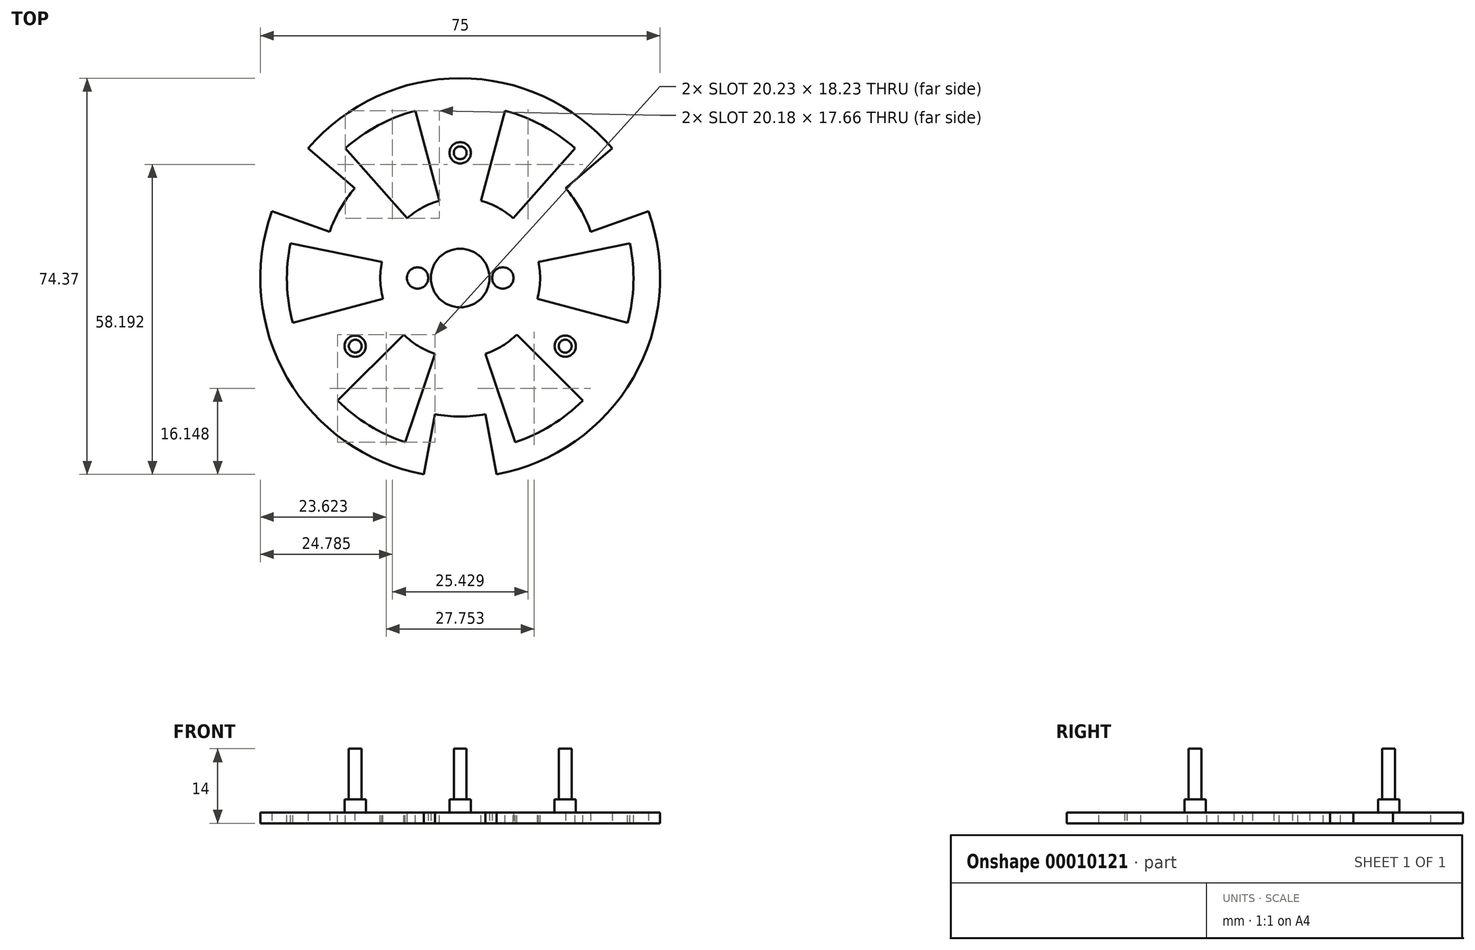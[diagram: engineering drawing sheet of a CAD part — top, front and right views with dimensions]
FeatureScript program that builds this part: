
annotation { "Feature Type Name" : "Feature", "Feature Type Description" : "" }
export const myFeature = defineFeature(function(context is Context, id is Id, definition is map)
    precondition{}
    {
        {
            var Q0;
            Q0=qCreatedBy(makeId("Top.planeOp"),FACE);
            var sketch = newSketch(context, id + "F0", { "sketchPlane" : qUnion([Q0])});
            skArc(sketch, "E0", {"start": v(6.83, -36.87) * mm, "mid": v(32.48, -18.75) * mm, "end": v(35.35, 12.52) * mm});
            skCircle(sketch, "E1", {"center": v(0, 0) * mm, "radius": 5.5 * mm});
            skLineSegment(sketch, "E2", {"start": v(0, 0) * mm, "end": v(-4.74, -25.56) * mm, "construction": true});
            skLineSegment(sketch, "E3", {"start": v(-4.74, -25.56) * mm, "end": v(-4.74, -25.56) * mm});
            skLineSegment(sketch, "E4", {"start": v(0, 0) * mm, "end": v(4.74, -25.56) * mm, "construction": true});
            skLineSegment(sketch, "E5", {"start": v(4.74, -25.56) * mm, "end": v(6.83, -36.87) * mm});
            skLineSegment(sketch, "E6", {"start": v(0, 0) * mm, "end": v(0, -37.5) * mm, "construction": true});
            skArc(sketch, "E7", {"start": v(-4.74, -25.56) * mm, "mid": v(0, -26) * mm, "end": v(4.74, -25.56) * mm});
            skLineSegment(sketch, "E8", {"start": v(-6.83, -36.87) * mm, "end": v(-4.74, -25.56) * mm});
            skLineSegment(sketch, "E9", {"start": v(-4.74, -25.56) * mm, "end": v(-6.83, -36.87) * mm, "construction": true});
            skLineSegment(sketch, "E10.1.0", {"start": v(35.35, 12.52) * mm, "end": v(24.5, 8.68) * mm});
            skLineSegment(sketch, "E10.1.1", {"start": v(24.5, 8.68) * mm, "end": v(24.5, 8.68) * mm});
            skLineSegment(sketch, "E10.1.2", {"start": v(24.5, 8.68) * mm, "end": v(24.5, 8.68) * mm});
            skArc(sketch, "E10.1.3", {"start": v(24.5, 8.68) * mm, "mid": v(22.52, 13) * mm, "end": v(19.77, 16.89) * mm});
            skLineSegment(sketch, "E10.1.4", {"start": v(19.77, 16.89) * mm, "end": v(28.52, 24.35) * mm});
            skLineSegment(sketch, "E10.2.0", {"start": v(-28.52, 24.35) * mm, "end": v(-19.77, 16.89) * mm});
            skLineSegment(sketch, "E10.2.1", {"start": v(-19.77, 16.89) * mm, "end": v(-19.77, 16.89) * mm});
            skLineSegment(sketch, "E10.2.2", {"start": v(-19.77, 16.89) * mm, "end": v(-19.77, 16.89) * mm});
            skArc(sketch, "E10.2.3", {"start": v(-19.77, 16.89) * mm, "mid": v(-22.52, 13) * mm, "end": v(-24.5, 8.68) * mm});
            skLineSegment(sketch, "E10.2.4", {"start": v(-24.5, 8.68) * mm, "end": v(-35.35, 12.52) * mm});
            skArc(sketch, "E11.trimOffspring", {"start": v(-35.35, 12.52) * mm, "mid": v(-32.48, -18.75) * mm, "end": v(-6.83, -36.87) * mm});
            skArc(sketch, "E12.trimOffspring", {"start": v(28.52, 24.35) * mm, "mid": v(0, 37.5) * mm, "end": v(-28.52, 24.35) * mm});
            skLineSegment(sketch, "E13", {"start": v(-6.83, -36.87) * mm, "end": v(0, -37.5) * mm, "construction": true});
            skLineSegment(sketch, "E14", {"start": v(6.83, -36.87) * mm, "end": v(0, -37.5) * mm, "construction": true});
            skCircle(sketch, "E15", {"center": v(-8, 0) * mm, "radius": 2 * mm});
            skLineSegment(sketch, "E16", {"start": v(0, 0) * mm, "end": v(-8, 0) * mm, "construction": true});
            skCircle(sketch, "E17.0.MirrorC", {"center": v(8, 0) * mm, "radius": 2 * mm});
            skSolve(sketch);
        }
        {
            var Q0;
            Q0 = qSketchRegion(id + "F0", true);
            extrude(context, id + "F1", {"entities" : qUnion([Q0]), "depth" : 2 * mm});
        }
        {
            var Q0;
            Q0=makeQuery(id+"F1.opExtrude","CAP_FACE",FACE,{"disambiguationData":[OSD([sQuery(id+"F0.wireOp",EDGE,"E0"),sQuery(id+"F0.wireOp",EDGE,"E1"),sQuery(id+"F0.wireOp",EDGE,"E5"),sQuery(id+"F0.wireOp",EDGE,"E7"),sQuery(id+"F0.wireOp",EDGE,"E8"),sQuery(id+"F0.wireOp",EDGE,"E3"),sQuery(id+"F0.wireOp",EDGE,"E10.1.0"),sQuery(id+"F0.wireOp",EDGE,"E10.1.1"),sQuery(id+"F0.wireOp",EDGE,"E10.1.3"),sQuery(id+"F0.wireOp",EDGE,"E10.1.4"),sQuery(id+"F0.wireOp",EDGE,"E10.2.0"),sQuery(id+"F0.wireOp",EDGE,"E10.2.1"),sQuery(id+"F0.wireOp",EDGE,"E10.2.3"),sQuery(id+"F0.wireOp",EDGE,"E10.2.4"),sQuery(id+"F0.wireOp",EDGE,"E11.trimOffspring"),sQuery(id+"F0.wireOp",EDGE,"E12.trimOffspring")])],"isStart":false});
            var sketch = newSketch(context, id + "F2", { "sketchPlane" : qUnion([Q0])});
            skCircle(sketch, "E18", {"center": v(0, 23.5) * mm, "radius": 2 * mm});
            skCircle(sketch, "E19.1.0", {"center": v(-19.7, -12.8) * mm, "radius": 2 * mm});
            skCircle(sketch, "E19.2.0", {"center": v(19.7, -12.8) * mm, "radius": 2 * mm});
            skPoint(sketch, "E19.center", {"position": v(0, 0) * mm});
            skLineSegment(sketch, "E20", {"start": v(0, 0) * mm, "end": v(0, 23.5) * mm, "construction": true});
            skLineSegment(sketch, "E21", {"start": v(0, 0) * mm, "end": v(19.7, -12.8) * mm, "construction": true});
            skLineSegment(sketch, "E22", {"start": v(0, 0) * mm, "end": v(-19.7, -12.8) * mm, "construction": true});
            skSolve(sketch);
        }
        {
            var Q0;
            Q0 = qSketchRegion(id + "F2", true);
            extrude(context, id + "F3", {"entities" : qUnion([Q0]), "operationType" : NewBodyOperationType.ADD, "depth" : 2.5 * mm});
        }
        {
            var Q0;
            Q0=makeQuery(id+"F3.opExtrude","CAP_FACE",FACE,{"disambiguationData":[OSD([sQuery(id+"F2.wireOp",EDGE,"E18")])],"isStart":false});
            var sketch = newSketch(context, id + "F4", { "sketchPlane" : qUnion([Q0])});
            skCircle(sketch, "E23", {"center": v(0, 23.5) * mm, "radius": 1.2 * mm});
            skCircle(sketch, "E24.1.0", {"center": v(-19.7, -12.8) * mm, "radius": 1.2 * mm});
            skCircle(sketch, "E24.2.0", {"center": v(19.7, -12.8) * mm, "radius": 1.2 * mm});
            skPoint(sketch, "E24.center", {"position": v(0, 0) * mm});
            skSolve(sketch);
        }
        {
            var Q0;
            Q0 = qSketchRegion(id + "F4", true);
            extrude(context, id + "F5", {"entities" : qUnion([Q0]), "operationType" : NewBodyOperationType.ADD, "depth" : 9.5 * mm});
        }
        {
            var Q0;
            Q0=makeQuery(id+"F1.opExtrude","CAP_FACE",FACE,{"disambiguationData":[OSD([sQuery(id+"F0.wireOp",EDGE,"E0"),sQuery(id+"F0.wireOp",EDGE,"E1"),sQuery(id+"F0.wireOp",EDGE,"E5"),sQuery(id+"F0.wireOp",EDGE,"E7"),sQuery(id+"F0.wireOp",EDGE,"E8"),sQuery(id+"F0.wireOp",EDGE,"E10.1.0"),sQuery(id+"F0.wireOp",EDGE,"E10.1.3"),sQuery(id+"F0.wireOp",EDGE,"E10.1.4"),sQuery(id+"F0.wireOp",EDGE,"E10.2.0"),sQuery(id+"F0.wireOp",EDGE,"E10.2.3"),sQuery(id+"F0.wireOp",EDGE,"E10.2.4"),sQuery(id+"F0.wireOp",EDGE,"E11.trimOffspring"),sQuery(id+"F0.wireOp",EDGE,"E12.trimOffspring"),sQuery(id+"F0.wireOp",EDGE,"E15"),sQuery(id+"F0.wireOp",EDGE,"E17.0.MirrorC")])],"isStart":false});
            var sketch = newSketch(context, id + "F6", { "sketchPlane" : qUnion([Q0])});
            skLineSegment(sketch, "E25", {"start": v(0, 0) * mm, "end": v(9.94, 11.23) * mm, "construction": true});
            skLineSegment(sketch, "E26", {"start": v(9.94, 11.23) * mm, "end": v(21.55, 24.35) * mm});
            skLineSegment(sketch, "E27", {"start": v(0, 0) * mm, "end": v(3.88, 14.49) * mm, "construction": true});
            skLineSegment(sketch, "E28", {"start": v(3.88, 14.49) * mm, "end": v(8.42, 31.4) * mm});
            skArc(sketch, "E29", {"start": v(21.55, 24.35) * mm, "mid": v(15.4, 28.64) * mm, "end": v(8.42, 31.4) * mm});
            skArc(sketch, "E30", {"start": v(9.94, 11.23) * mm, "mid": v(7.1, 13.21) * mm, "end": v(3.88, 14.49) * mm});
            skLineSegment(sketch, "E31", {"start": v(0, 0) * mm, "end": v(-3.88, 14.49) * mm, "construction": true});
            skLineSegment(sketch, "E32", {"start": v(-3.88, 14.49) * mm, "end": v(-8.42, 31.4) * mm});
            skLineSegment(sketch, "E33", {"start": v(0, 0) * mm, "end": v(-9.94, 11.23) * mm, "construction": true});
            skLineSegment(sketch, "E34", {"start": v(-9.94, 11.23) * mm, "end": v(-21.55, 24.35) * mm});
            skArc(sketch, "E35", {"start": v(-8.42, 31.4) * mm, "mid": v(-15.4, 28.64) * mm, "end": v(-21.55, 24.35) * mm});
            skArc(sketch, "E36", {"start": v(-3.88, 14.49) * mm, "mid": v(-7.1, 13.21) * mm, "end": v(-9.94, 11.23) * mm});
            skLineSegment(sketch, "E37", {"start": v(-8.42, 31.4) * mm, "end": v(0, 31.4) * mm, "construction": true});
            skLineSegment(sketch, "E38", {"start": v(0, 31.4) * mm, "end": v(8.42, 31.4) * mm, "construction": true});
            skLineSegment(sketch, "E39", {"start": v(-28.52, 24.35) * mm, "end": v(-21.55, 24.35) * mm, "construction": true});
            skLineSegment(sketch, "E40", {"start": v(21.55, 24.35) * mm, "end": v(28.52, 24.35) * mm, "construction": true});
            skArc(sketch, "E41.1.0", {"start": v(-10.6, -10.6) * mm, "mid": v(-7.9, -12.76) * mm, "end": v(-4.76, -14.22) * mm});
            skArc(sketch, "E41.1.1", {"start": v(-14.7, 3) * mm, "mid": v(-15, -0.46) * mm, "end": v(-14.49, -3.88) * mm});
            skLineSegment(sketch, "E41.1.2", {"start": v(-14.49, -3.88) * mm, "end": v(-31.4, -8.42) * mm});
            skLineSegment(sketch, "E41.1.3", {"start": v(-10.6, -10.6) * mm, "end": v(-23, -23) * mm});
            skLineSegment(sketch, "E41.1.4", {"start": v(-4.76, -14.22) * mm, "end": v(-10.32, -30.84) * mm});
            skLineSegment(sketch, "E41.1.5", {"start": v(-14.7, 3) * mm, "end": v(-31.86, 6.48) * mm});
            skArc(sketch, "E41.1.6", {"start": v(-23, -23) * mm, "mid": v(-17.11, -27.65) * mm, "end": v(-10.32, -30.84) * mm});
            skArc(sketch, "E41.1.7", {"start": v(-31.86, 6.48) * mm, "mid": v(-32.5, -1) * mm, "end": v(-31.4, -8.42) * mm});
            skArc(sketch, "E41.2.0", {"start": v(14.49, -3.88) * mm, "mid": v(15, -0.46) * mm, "end": v(14.7, 3) * mm});
            skArc(sketch, "E41.2.1", {"start": v(4.76, -14.22) * mm, "mid": v(7.9, -12.76) * mm, "end": v(10.6, -10.6) * mm});
            skLineSegment(sketch, "E41.2.2", {"start": v(10.6, -10.6) * mm, "end": v(23, -23) * mm});
            skLineSegment(sketch, "E41.2.3", {"start": v(14.49, -3.88) * mm, "end": v(31.4, -8.42) * mm});
            skLineSegment(sketch, "E41.2.4", {"start": v(14.7, 3) * mm, "end": v(31.86, 6.48) * mm});
            skLineSegment(sketch, "E41.2.5", {"start": v(4.76, -14.22) * mm, "end": v(10.32, -30.84) * mm});
            skArc(sketch, "E41.2.6", {"start": v(31.4, -8.42) * mm, "mid": v(32.5, -1) * mm, "end": v(31.86, 6.48) * mm});
            skArc(sketch, "E41.2.7", {"start": v(10.32, -30.84) * mm, "mid": v(17.11, -27.65) * mm, "end": v(23, -23) * mm});
            skSolve(sketch);
        }
        {
            var Q0;
            Q0 = qSketchRegion(id + "F6", true);
            extrude(context, id + "F7", {"entities" : qUnion([Q0]), "operationType" : NewBodyOperationType.REMOVE, "endBound" : BoundingType.UP_TO_NEXT, "oppositeDirection" : true, "depth" : 25 * mm});
        }
    });
